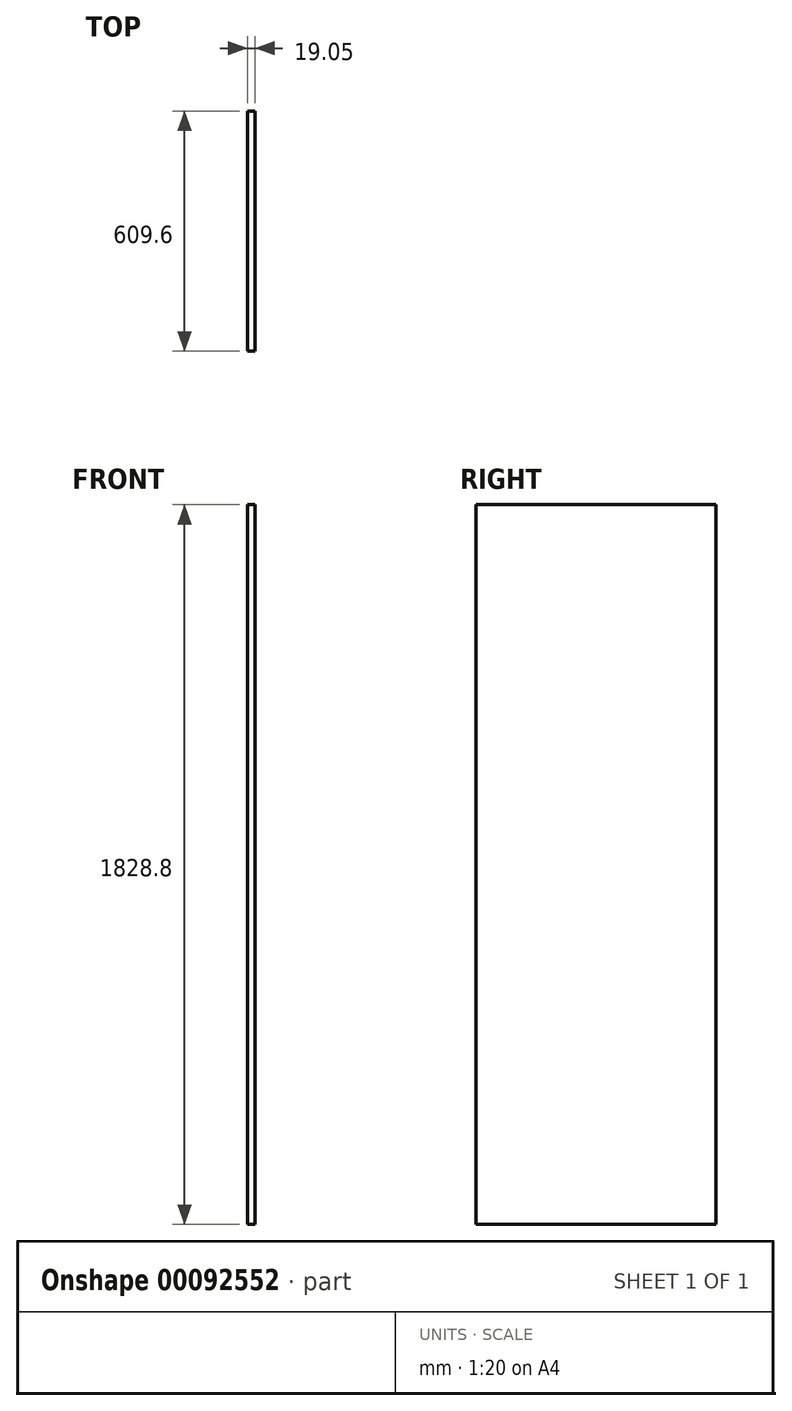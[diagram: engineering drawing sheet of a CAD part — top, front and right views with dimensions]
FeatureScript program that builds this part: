
annotation { "Feature Type Name" : "Feature", "Feature Type Description" : "" }
export const myFeature = defineFeature(function(context is Context, id is Id, definition is map)
    precondition{}
    {
        {
            var Q0;
            Q0=qCreatedBy(makeId("Right.planeOp"),FACE);
            var sketch = newSketch(context, id + "F0", { "sketchPlane" : qUnion([Q0])});
            skLineSegment(sketch, "E0.bottom", {"start": v(-221.42, 914.66) * mm, "end": v(-831.02, 914.66) * mm});
            skLineSegment(sketch, "E0.top", {"start": v(-221.42, -914.14) * mm, "end": v(-831.02, -914.14) * mm});
            skLineSegment(sketch, "E0.left", {"start": v(-221.42, 914.66) * mm, "end": v(-221.42, -914.14) * mm});
            skLineSegment(sketch, "E0.right", {"start": v(-831.02, 914.66) * mm, "end": v(-831.02, -914.14) * mm});
            skSolve(sketch);
        }
        {
            var Q0;
            Q0=makeQuery(id+"F0.imprint","IMPRINT",FACE,{"disambiguationData":[TD([[makeQuery(id+"F0.imprint","IMPRINT",EDGE,{"derivedFrom":sQuery(id+"F0.wireOp",EDGE,"E0.bottom")}),1.0]])]});
            extrude(context, id + "F1", {"entities" : qUnion([Q0]), "depth" : 19.05 * mm});
        }
    });
